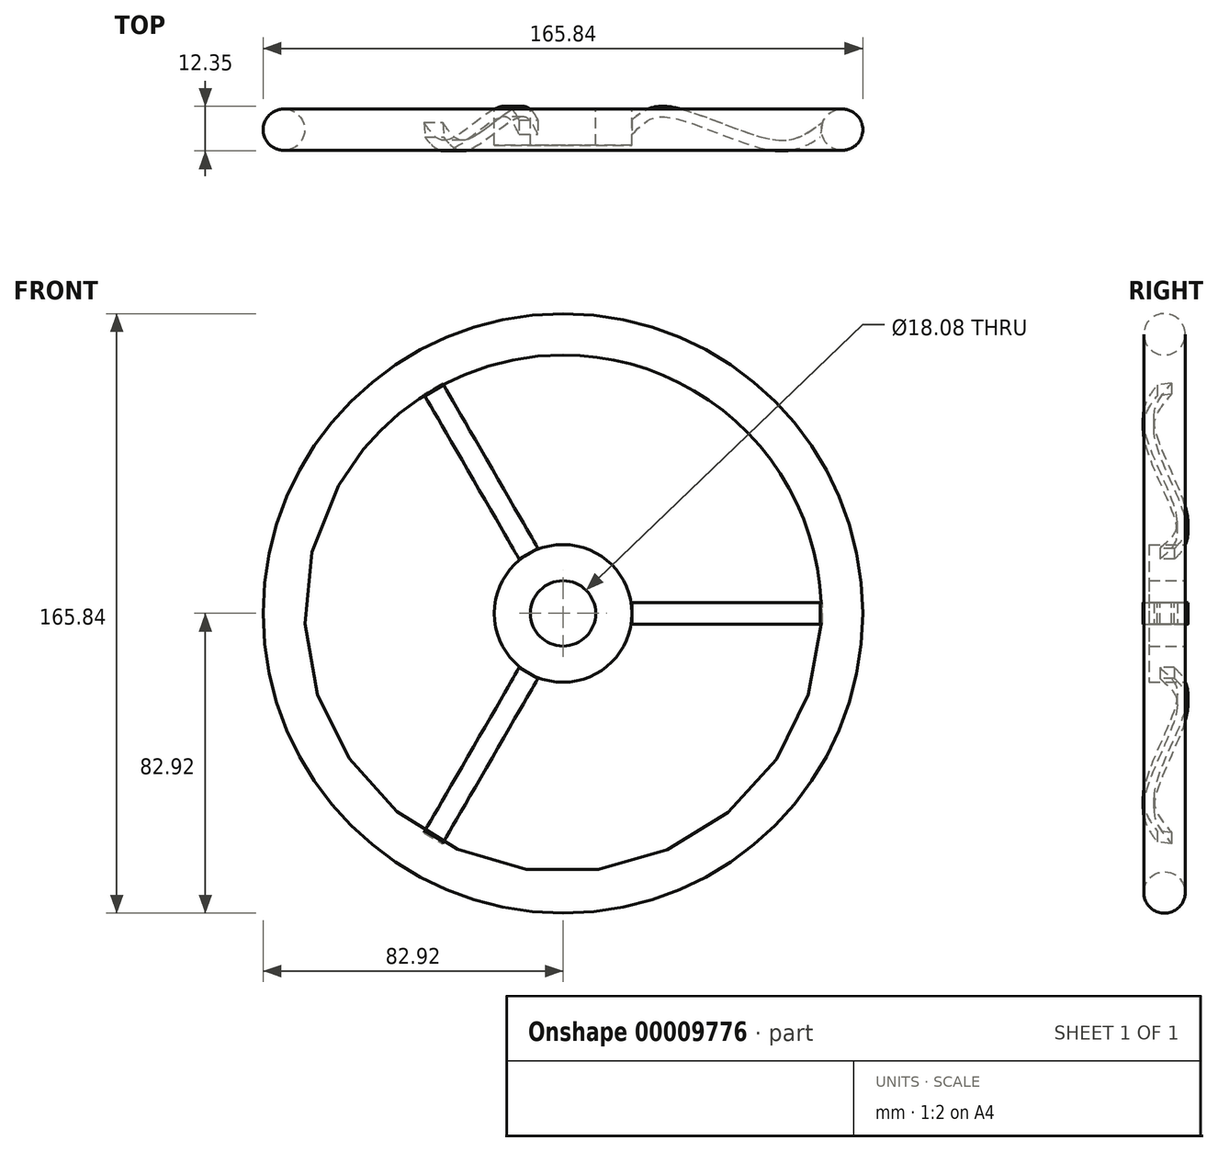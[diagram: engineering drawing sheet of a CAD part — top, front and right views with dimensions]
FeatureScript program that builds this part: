
annotation { "Feature Type Name" : "Feature", "Feature Type Description" : "" }
export const myFeature = defineFeature(function(context is Context, id is Id, definition is map)
    precondition{}
    {
        {
            var Q0;
            Q0=qCreatedBy(makeId("Top.planeOp"),FACE);
            var sketch = newSketch(context, id + "F0", { "sketchPlane" : qUnion([Q0])});
            skLineSegment(sketch, "E0.bottom", {"start": v(9.04, 5.73) * mm, "end": v(19.04, 5.73) * mm});
            skLineSegment(sketch, "E0.top", {"start": v(9.04, -4.27) * mm, "end": v(19.04, -4.27) * mm});
            skLineSegment(sketch, "E0.left", {"start": v(9.04, 5.73) * mm, "end": v(9.04, -4.27) * mm});
            skLineSegment(sketch, "E0.right", {"start": v(19.04, 5.73) * mm, "end": v(19.04, -4.27) * mm});
            skLineSegment(sketch, "E1", {"start": v(0, 26.16) * mm, "end": v(0, -51.19) * mm, "construction": true});
            skCircle(sketch, "E2", {"center": v(77.2, 0) * mm, "radius": 5.73 * mm});
            skFitSpline(sketch, "E3", {"points": [v(19.04, 0.73) * mm, v(28.15, 4.93) * mm, v(58.86, -4.27) * mm, v(71.47, 0) * mm], "startDerivative": vector(28.07, 26) * mm, "endDerivative": vector(35.56, 24.76) * mm});
            skSolve(sketch);
        }
        {
            var Q0;
            Q0=makeQuery(id+"F0.imprint","IMPRINT",FACE,{"disambiguationData":[TD([[makeQuery(id+"F0.imprint","IMPRINT",EDGE,{"derivedFrom":sQuery(id+"F0.wireOp",EDGE,"E2")}),1.0]])]});
            var Q1;
            Q1=makeQuery(id+"F0.imprint","IMPRINT",FACE,{"disambiguationData":[TD([[makeQuery(id+"F0.imprint","IMPRINT",EDGE,{"derivedFrom":sQuery(id+"F0.wireOp",EDGE,"E0.bottom")}),-1.0]])]});
            var Q2;
            Q2=sQuery(id+"F0.wireOp",EDGE,"E2");
            var Q3;
            Q3=sQuery(id+"F0.wireOp",EDGE,"E1");
            revolve(context, id + "F1", {"entities" : qUnion([Q0, Q1]), "surfaceEntities" : qUnion([Q2]), "axis" : qUnion([Q3]), "revolveType" : RevolveType.FULL});
        }
        {
            var Q0;
            Q0=qCreatedBy(makeId("Right.planeOp"),FACE);
            var Q1;
            Q1=sQuery(id+"F0.wireOp",VERTEX,"E3.0.internal");
            cPlane(context, id + "F2", {"entities" : qUnion([Q0, Q1]), "cplaneType" : CPlaneType.PLANE_POINT, "offset" : 150 * mm, "width" : 150 * mm, "height" : 150 * mm});
        }
        {
            var Q0;
            Q0=qCreatedBy(id+"F2.planeOp",FACE);
            var sketch = newSketch(context, id + "F3", { "sketchPlane" : qUnion([Q0])});
            skPoint(sketch, "E4.0", {"position": v(0.73, 0) * mm});
            skLineSegment(sketch, "E5.rect.bottom", {"start": v(2.73, -3) * mm, "end": v(-1.27, -3) * mm});
            skLineSegment(sketch, "E5.rect.top", {"start": v(2.73, 3) * mm, "end": v(-1.27, 3) * mm});
            skLineSegment(sketch, "E5.rect.left", {"start": v(2.73, -3) * mm, "end": v(2.73, 3) * mm});
            skLineSegment(sketch, "E5.rect.right", {"start": v(-1.27, -3) * mm, "end": v(-1.27, 3) * mm});
            skSolve(sketch);
        }
        {
            var Q0;
            Q0=makeQuery(id+"F3.imprint","IMPRINT",FACE,{"disambiguationData":[TD([[makeQuery(id+"F3.imprint","IMPRINT",EDGE,{"derivedFrom":sQuery(id+"F3.wireOp",EDGE,"E5.rect.bottom")}),-1.0]])]});
            var Q1;
            Q1=sQuery(id+"F0.wireOp",EDGE,"E3");
            sweep(context, id + "F4", {"profiles" : qUnion([Q0]), "path" : qUnion([Q1])});
        }
        {
            var Q0;
            Q0=makeQuery(id+"F4.opSweep","SWEPT_BODY",BODY,{"disambiguationData":[OSD([sQuery(id+"F0.wireOp",EDGE,"E3"),sQuery(id+"F3.wireOp",EDGE,"E5.rect.bottom"),sQuery(id+"F3.wireOp",EDGE,"E5.rect.top"),sQuery(id+"F3.wireOp",EDGE,"E5.rect.left"),sQuery(id+"F3.wireOp",EDGE,"E5.rect.right")])]});
            var Q1;
            Q1=makeQuery(id+"F1.opRevolve","SWEPT_FACE",FACE,{"disambiguationData":[OSD([sQuery(id+"F0.wireOp",EDGE,"E0.right")])]});
            circularPattern(context, id + "F5", {"entities" : qUnion([Q0]), "axis" : qUnion([Q1]), "angle" : 120 * degree, "instanceCount" : 3});
        }
    });
